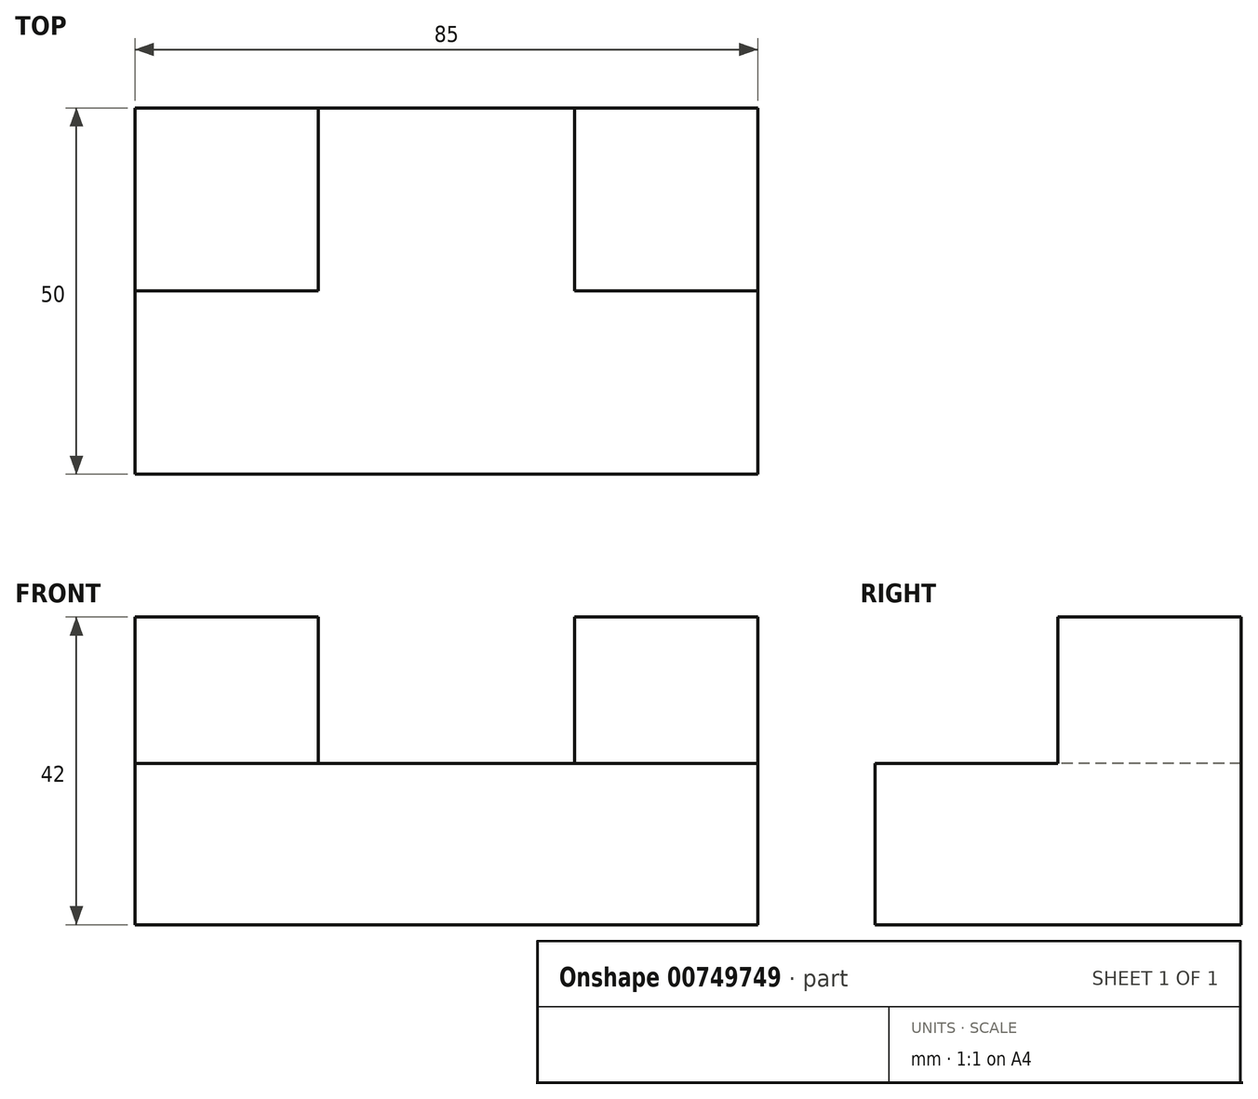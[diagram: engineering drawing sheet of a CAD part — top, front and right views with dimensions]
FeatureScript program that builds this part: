
annotation { "Feature Type Name" : "Feature", "Feature Type Description" : "" }
export const myFeature = defineFeature(function(context is Context, id is Id, definition is map)
    precondition{}
    {
        {
            var Q0;
            Q0=qCreatedBy(makeId("Front.planeOp"),FACE);
            var sketch = newSketch(context, id + "F0", { "sketchPlane" : qUnion([Q0])});
            skLineSegment(sketch, "E0.bottom", {"start": v(0, 0) * mm, "end": v(85, 0) * mm});
            skLineSegment(sketch, "E0.top", {"start": v(0, 22) * mm, "end": v(85, 22) * mm});
            skLineSegment(sketch, "E0.left", {"start": v(0, 0) * mm, "end": v(0, 22) * mm});
            skLineSegment(sketch, "E0.right", {"start": v(85, 0) * mm, "end": v(85, 22) * mm});
            skSolve(sketch);
        }
        {
            var Q0;
            Q0 = qSketchRegion(id + "F0", true);
            extrude(context, id + "F1", {"entities" : qUnion([Q0]), "depth" : 50 * mm, "offsetDistance" : 25 * mm});
        }
        {
            var Q0;
            Q0=makeQuery(id+"F1.opExtrude","SWEPT_FACE",FACE,{"disambiguationData":[OSD([sQuery(id+"F0.wireOp",EDGE,"E0.top")])]});
            var sketch = newSketch(context, id + "F2", { "sketchPlane" : qUnion([Q0])});
            skLineSegment(sketch, "E1.bottom", {"start": v(0, 0) * mm, "end": v(25, 0) * mm});
            skLineSegment(sketch, "E1.top", {"start": v(0, -25) * mm, "end": v(25, -25) * mm});
            skLineSegment(sketch, "E1.left", {"start": v(0, 0) * mm, "end": v(0, -25) * mm});
            skLineSegment(sketch, "E1.right", {"start": v(25, 0) * mm, "end": v(25, -25) * mm});
            skLineSegment(sketch, "E2.bottom", {"start": v(85, 0) * mm, "end": v(60, 0) * mm});
            skLineSegment(sketch, "E2.top", {"start": v(85, -25) * mm, "end": v(60, -25) * mm});
            skLineSegment(sketch, "E2.left", {"start": v(85, 0) * mm, "end": v(85, -25) * mm});
            skLineSegment(sketch, "E2.right", {"start": v(60, 0) * mm, "end": v(60, -25) * mm});
            skSolve(sketch);
        }
        {
            var Q0;
            Q0=makeQuery(id+"F2.imprint","IMPRINT",FACE,{"disambiguationData":[TD([[makeQuery(id+"F2.imprint","IMPRINT",EDGE,{"derivedFrom":sQuery(id+"F2.wireOp",EDGE,"E2.bottom")}),-1.0]])]});
            var Q1;
            Q1=makeQuery(id+"F2.imprint","IMPRINT",FACE,{"disambiguationData":[TD([[makeQuery(id+"F2.imprint","IMPRINT",EDGE,{"derivedFrom":sQuery(id+"F2.wireOp",EDGE,"E1.bottom")}),-1.0]])]});
            extrude(context, id + "F3", {"entities" : qUnion([Q0, Q1]), "operationType" : NewBodyOperationType.ADD, "depth" : 20 * mm, "offsetDistance" : 25 * mm});
        }
    });
